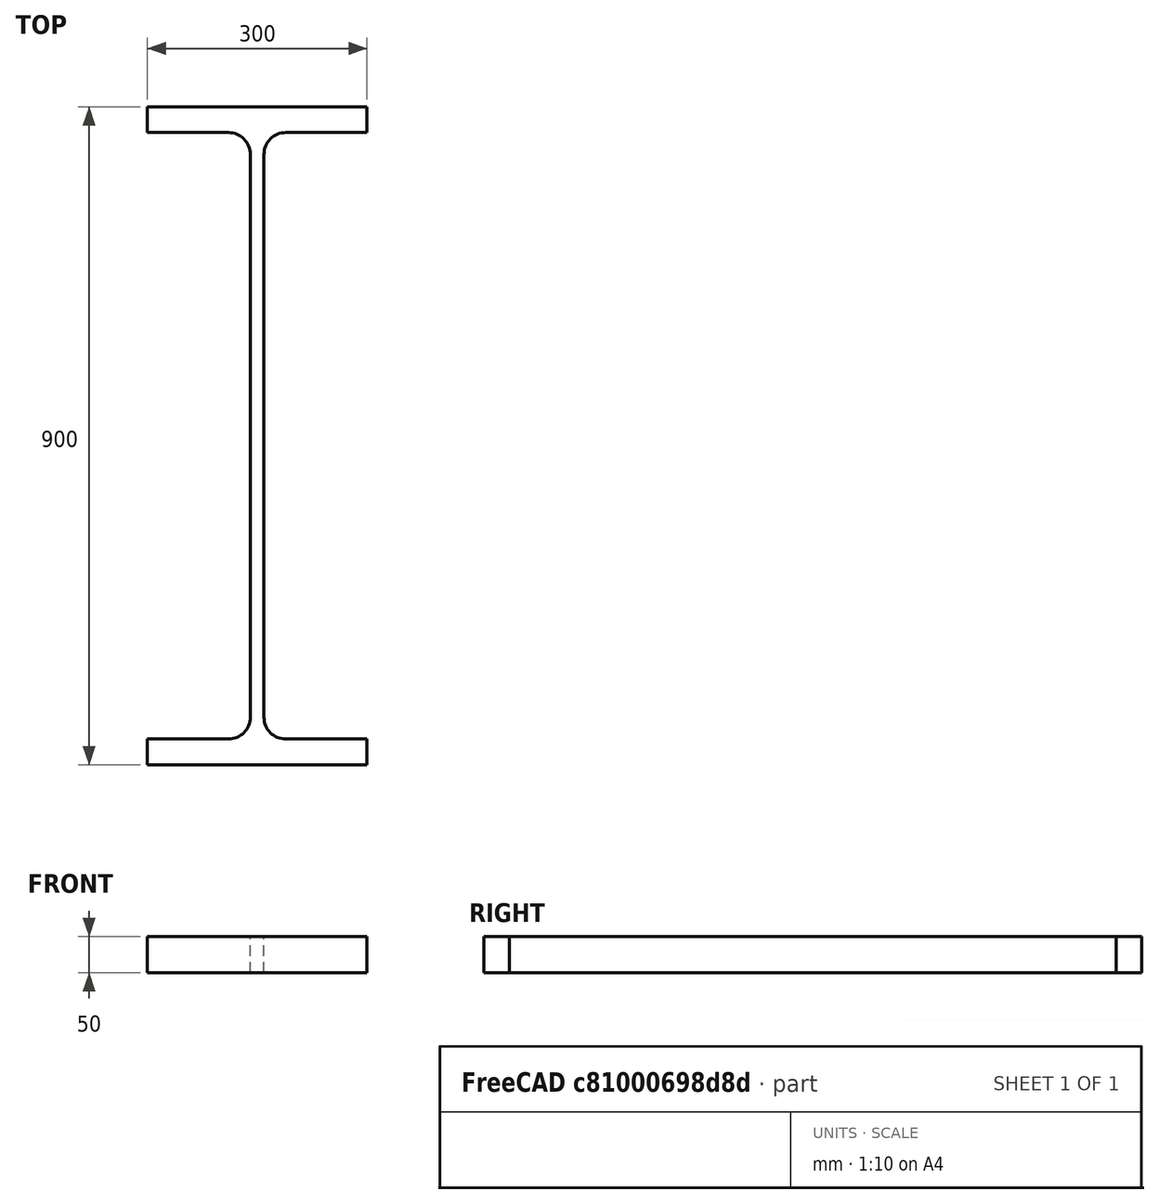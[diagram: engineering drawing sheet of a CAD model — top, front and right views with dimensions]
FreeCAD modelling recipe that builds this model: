
FCSTD DOCUMENT  (FreeCAD 0.15R4671 (Git))
Label: HE-B-Profile 900 DIN1025-2 S235JR
License: All rights reserved
LicenseURL: http://en.wikipedia.org/wiki/All_rights_reserved
objects: Sketcher::SketchObject×1, Part::Extrusion×1
note: 2 computed .brp shape members not serialized (recipe doc carries the construction recipe); baked Part::Feature solids carry a one-line shape summary decoded from their .brp

FEATURE [Sketcher::SketchObject] Sketch
  sketch-geometry (16):
    g0: LineSegment StartX=9.25 StartY=-385 StartZ=0 EndX=9.25 EndY=385 EndZ=0
    g1: LineSegment StartX=39.25 StartY=415 StartZ=0 EndX=150 EndY=415 EndZ=0
    g2: LineSegment StartX=150 StartY=415 StartZ=0 EndX=150 EndY=450 EndZ=0
    g3: LineSegment StartX=150 StartY=450 StartZ=0 EndX=-150 EndY=450 EndZ=0
    g4: LineSegment StartX=-150 StartY=450 StartZ=0 EndX=-150 EndY=415 EndZ=0
    g5: LineSegment StartX=-150 StartY=415 StartZ=0 EndX=-39.25 EndY=415 EndZ=0
    g6: LineSegment StartX=-9.25 StartY=385 StartZ=0 EndX=-9.25 EndY=-385 EndZ=0
    g7: LineSegment StartX=-39.25 StartY=-415 StartZ=0 EndX=-150 EndY=-415 EndZ=0
    g8: LineSegment StartX=-150 StartY=-415 StartZ=0 EndX=-150 EndY=-450 EndZ=0
    g9: LineSegment StartX=-150 StartY=-450 StartZ=0 EndX=150 EndY=-450 EndZ=0
    g10: LineSegment StartX=150 StartY=-450 StartZ=0 EndX=150 EndY=-415 EndZ=0
    g11: LineSegment StartX=150 StartY=-415 StartZ=0 EndX=39.25 EndY=-415 EndZ=0
    g12: ArcOfCircle CenterX=39.25 CenterY=385 CenterZ=0 NormalX=0 NormalY=0 NormalZ=1 Radius=30 StartAngle=1.5708 EndAngle=3.14159
    g13: ArcOfCircle CenterX=39.25 CenterY=-385 CenterZ=0 NormalX=0 NormalY=0 NormalZ=1 Radius=30 StartAngle=3.14159 EndAngle=4.71239
    g14: ArcOfCircle CenterX=-39.25 CenterY=385 CenterZ=0 NormalX=0 NormalY=0 NormalZ=1 Radius=30 StartAngle=0 EndAngle=1.5708
    g15: ArcOfCircle CenterX=-39.25 CenterY=-385 CenterZ=0 NormalX=0 NormalY=0 NormalZ=1 Radius=30 StartAngle=4.71239 EndAngle=6.28319
  constraints (42):
    c: Vertical(g0)
    c: Coincident(g2,g1)
    c: Vertical(g2)
    c: Coincident(g3,g2)
    c: Coincident(g4,g3)
    c: Vertical(g4)
    c: Coincident(g5,g4)
    c: Horizontal(g5)
    c: Vertical(g6)
    c: Horizontal(g7)
    c: Coincident(g8,g7)
    c: Vertical(g8)
    c: Coincident(g9,g8)
    c: Horizontal(g9)
    c: Coincident(g10,g9)
    c: Vertical(g10)
    c: Coincident(g11,g10)
    c: Horizontal(g11)
    c: Tangent(g1,g12) = 1.5708
    c: Tangent(g0,g12) = 1.5708
    c: Tangent(g0,g13) = 1.5708
    c: Tangent(g11,g13) = 1.5708
    c: Tangent(g5,g14) = 1.5708
    c: Tangent(g6,g14) = 1.5708
    c: Tangent(g6,g15) = 1.5708
    c: Tangent(g7,g15) = 1.5708
    c: Equal(g3,g9)
    c: Equal(g2,g4)
    c: Equal(g4,g8)
    c: Equal(g8,g10)
    c: Equal(g12,g14)
    c: Equal(g14,g15)
    c: Equal(g15,g13)
    c: Symmetric(g2,g3,g-2)
    c: Symmetric(g9,g8,g-2)
    c: Symmetric(g0,g6,g-2)
    c: Symmetric(g2,g9,g-1)
    c: DistanceY(g2,g9) = -900
    c: DistanceX(g3) = -300
    c: DistanceX(g0,g6) = -18.5
    c: DistanceY(g2) = 35
    c: Radius(g12) = 30
FEATURE [Part::Extrusion] Extrude  label="HE-B-Profile 900 DIN1025-2 S235JR"
  Base = -> Sketch
  Dir = (0,0,50)
  Solid = true
